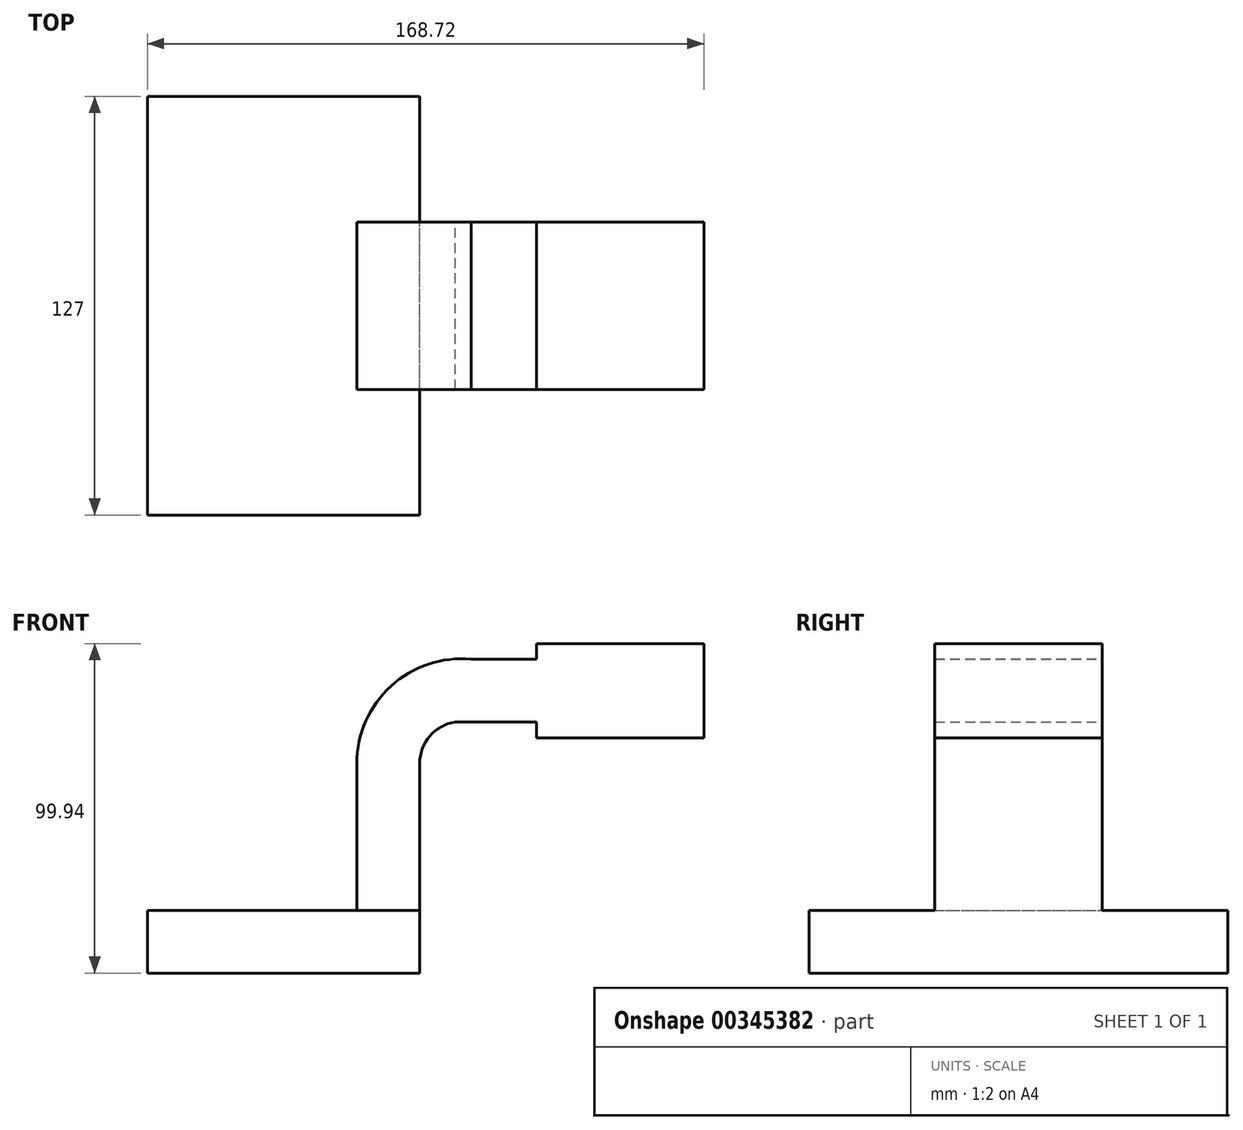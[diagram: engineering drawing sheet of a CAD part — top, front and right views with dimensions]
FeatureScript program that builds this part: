
annotation { "Feature Type Name" : "Feature", "Feature Type Description" : "" }
export const myFeature = defineFeature(function(context is Context, id is Id, definition is map)
    precondition{}
    {
        {
            var Q0;
            Q0=qCreatedBy(makeId("Front.planeOp"),FACE);
            var sketch = newSketch(context, id + "F0", { "sketchPlane" : qUnion([Q0])});
            skLineSegment(sketch, "E0.bottom", {"start": v(-61.24, -25.8) * mm, "end": v(21.31, -25.8) * mm});
            skLineSegment(sketch, "E0.top", {"start": v(-61.24, -44.85) * mm, "end": v(21.31, -44.85) * mm});
            skLineSegment(sketch, "E0.left", {"start": v(-61.24, -25.8) * mm, "end": v(-61.24, -44.85) * mm});
            skLineSegment(sketch, "E0.right", {"start": v(21.31, -25.8) * mm, "end": v(21.31, -44.85) * mm});
            skLineSegment(sketch, "E1.bottom", {"start": v(107.48, 26.51) * mm, "end": v(56.68, 26.51) * mm});
            skLineSegment(sketch, "E1.top", {"start": v(107.48, 55.09) * mm, "end": v(56.68, 55.09) * mm});
            skLineSegment(sketch, "E1.left", {"start": v(107.48, 26.51) * mm, "end": v(107.48, 55.09) * mm});
            skLineSegment(sketch, "E1.right", {"start": v(56.68, 26.51) * mm, "end": v(56.68, 55.09) * mm});
            skPoint(sketch, "E1.middle", {"position": v(82.08, 40.8) * mm});
            skLineSegment(sketch, "E2", {"start": v(21.31, -25.8) * mm, "end": v(21.31, 18.74) * mm});
            skArc(sketch, "E3", {"start": v(21.31, 18.74) * mm, "mid": v(24.39, 27.03) * mm, "end": v(32.13, 31.3) * mm});
            skLineSegment(sketch, "E4", {"start": v(32.13, 31.3) * mm, "end": v(78.23, 31.3) * mm});
            skLineSegment(sketch, "E5.0", {"start": v(36.99, 50.35) * mm, "end": v(78.23, 50.35) * mm});
            skArc(sketch, "E5.1", {"start": v(2.26, 18.74) * mm, "mid": v(12.64, 42.22) * mm, "end": v(36.99, 50.35) * mm});
            skLineSegment(sketch, "E5.2", {"start": v(2.26, -25.8) * mm, "end": v(2.26, 18.74) * mm});
            skLineSegment(sketch, "E6", {"start": v(78.23, 26.51) * mm, "end": v(78.23, 55.09) * mm});
            skFitSpline(sketch, "E7", {"points": [v(-61.24, -25.8) * mm, v(56.68, 55.09) * mm], "startDerivative": vector(-4.22, 144.5) * mm, "endDerivative": vector(226.3, -8.14) * mm});
            skSolve(sketch);
        }
        {
            var Q0;
            Q0=makeQuery(id+"F0.imprint","IMPRINT",FACE,{"disambiguationData":[TD([[makeQuery(id+"F0.imprint","IMPRINT",EDGE,{"derivedFrom":sQuery(id+"F0.wireOp",EDGE,"E0.top")}),1.0]])]});
            extrude(context, id + "F1", {"entities" : qUnion([Q0]), "endBound" : BoundingType.SYMMETRIC, "depth" : 127 * mm});
        }
        {
            var Q0;
            {var subQ1=sQuery(id+"F0.wireOp",EDGE,"E2");Q0=makeQuery(id+"F0.imprint","IMPRINT",FACE,{"disambiguationData":[TD([[makeQuery(id+"F0.imprint","IMPRINT",EDGE,{"derivedFrom":subQ1}),1.0]])]});}
            var Q1;
            {var subQ0=sQuery(id+"F0.wireOp",EDGE,"E4");var subQ1=sQuery(id+"F0.wireOp",EDGE,"E1.right");var subQ2=makeQuery(id+"F0.imprint","INTERSECT",VERTEX,{"derivedFrom":[subQ1,subQ0]});Q1=makeQuery(id+"F0.imprint","IMPRINT",FACE,{"disambiguationData":[TD([[makeQuery(id+"F0.imprint","IMPRINT",EDGE,{"disambiguationData":[TD([[subQ2,-1.0]])],"derivedFrom":subQ1}),-1.0]])]});}
            var Q2;
            {var subQ4=sQuery(id+"F0.wireOp",EDGE,"E1.left");Q2=makeQuery(id+"F0.imprint","IMPRINT",FACE,{"disambiguationData":[TD([[makeQuery(id+"F0.imprint","IMPRINT",EDGE,{"derivedFrom":subQ4}),1.0]])]});}
            var Q3;
            {var subQ3=sQuery(id+"F0.wireOp",EDGE,"E6");var subQ5=sQuery(id+"F0.wireOp",EDGE,"E5.0");var subQ6=makeQuery(id+"F0.imprint","INTERSECT",VERTEX,{"derivedFrom":[subQ5,subQ3]});Q3=makeQuery(id+"F0.imprint","IMPRINT",FACE,{"disambiguationData":[TD([[makeQuery(id+"F0.imprint","IMPRINT",EDGE,{"disambiguationData":[TD([[subQ6,1.0]])],"derivedFrom":subQ5}),1.0]])]});}
            var Q4;
            {var subQ0=sQuery(id+"F0.wireOp",EDGE,"E1.right");var subQ1=sQuery(id+"F0.wireOp",EDGE,"E1.bottom");var subQ2=makeQuery(id+"F0.imprint","INTERSECT",VERTEX,{"derivedFrom":[subQ1,subQ0]});Q4=makeQuery(id+"F0.imprint","IMPRINT",FACE,{"disambiguationData":[TD([[makeQuery(id+"F0.imprint","IMPRINT",EDGE,{"disambiguationData":[TD([[subQ2,1.0]])],"derivedFrom":subQ1}),-1.0]])]});}
            extrude(context, id + "F2", {"entities" : qUnion([Q0, Q1, Q2, Q3, Q4]), "operationType" : NewBodyOperationType.ADD, "endBound" : BoundingType.SYMMETRIC, "depth" : 50.8 * mm});
        }
        {
            var Q0;
            {var subQ0=sQuery(id+"F0.wireOp",EDGE,"E5.1");Q0=makeQuery(id+"F0.imprint","IMPRINT",FACE,{"disambiguationData":[TD([[makeQuery(id+"F0.imprint","IMPRINT",EDGE,{"derivedFrom":subQ0}),1.0]])]});}
            extrude(context, id + "F3", {"entities" : qUnion([Q0]), "operationType" : NewBodyOperationType.ADD, "endBound" : BoundingType.SYMMETRIC, "depth" : 15.88 * mm});
        }
    });
